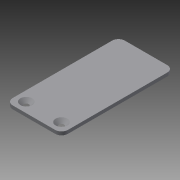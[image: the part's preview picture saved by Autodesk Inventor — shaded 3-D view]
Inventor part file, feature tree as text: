
AUTODESK INVENTOR PART (.ipt)
format: ipt  version: 2014 (Build 180170000, 170)  size: 128,512 bytes
history: native  units: mm
features: sketch x6, extrude x5, reference x3, chamfer x1, plane x1
ambient origin geometry x8: Origin, YZ Plane, XZ Plane, XY Plane, X Axis, Y Axis, Z Axis, Center Point
bodies: Solid1 (feature_tree)
feature tree (16):
  extrude  "Extrusion1"  Depth=1.6mm TaperAngle=0.0deg
  extrude  "Extrusion2"  Depth=3.0mm TaperAngle=0.0deg
  chamfer  "Chamfer1"  Distance=3.0mm
  sketch  "Sketch3"  dims[d13=-3.0mm d14=20.0mm d15=0.0mm]
  extrude  "Extrusion4"  Depth=20.0mm TaperAngle=0.0deg
  extrude  "Extrusion5"  [1 undecoded]
  plane  "Work Plane1"
  extrude  "Extrusion6"  [1 undecoded]
  sketch  "Sketch1"  dims[d0=1.6mm d1=0.0mm d2=1.6mm d3=0.0mm]
  reference  "Reference1"
  sketch  "Sketch2"  dims[d4=1.6mm d5=2.0mm d6=45.0deg d9=3.0mm d10=0.0mm d11=3.0mm d12=0.0mm]
  reference  "Reference2"
  reference  "Reference3"
  sketch  "Sketch6"
  sketch  "Sketch7"
  sketch  "Sketch8"
note: 2 required parameter values undecoded (feature->parameter linkage not recoverable at this tier; creation-order binding heuristic only, values carry confidence <= 0.55)
